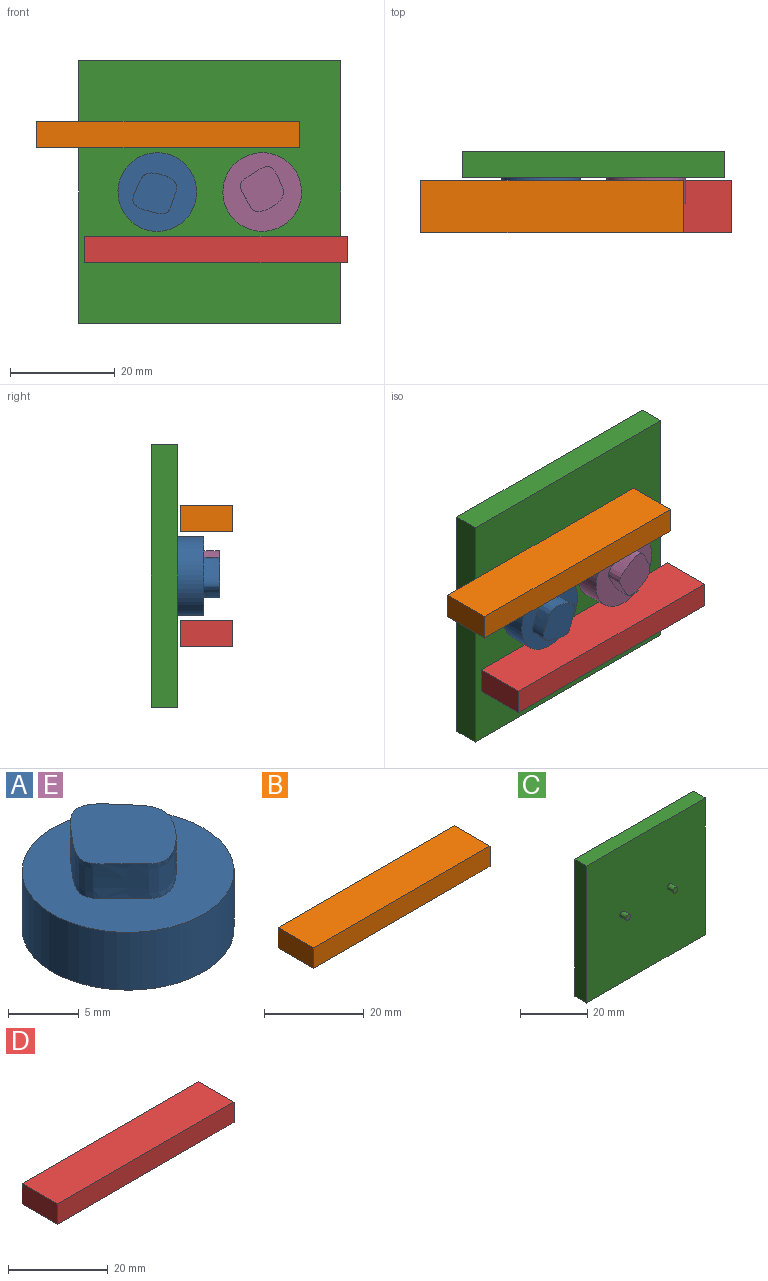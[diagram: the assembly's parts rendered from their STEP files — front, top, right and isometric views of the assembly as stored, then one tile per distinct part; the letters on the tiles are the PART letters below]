
ASSEMBLY  parts=5 mates=4
PART A: 7 faces, bbox 15x15x8 mm
  f0: cylinder r=7.5mm len=15mm, axis (0,0,-1), area 235.6mm2, adj f1,f2
  f1: plane 15x15mm, normal (0,0,1), area 127.5mm2, adj f0,f3
  f2: plane 15x15mm, normal (0,0,-1), area 173.6mm2, adj f0,f5
  f3: extruded ~8.88x8.32mm, area 76.5mm2, adj f1,f4
  f4: plane 9.28x8.73mm, normal (0,0,1), area 49.2mm2, adj f3
  f5: cylinder r=1mm len=2mm, axis (0,0,-1), area 12.6mm2, adj f2,f6
  f6: plane 2x2mm, normal (0,0,-1), area 3.1mm2, adj f5
PART B: 6 faces, bbox 50x10x5 mm
  f0: plane 50x5mm, normal (0,-1,0), area 250mm2, adj f1,f3,f4,f5
  f1: plane 10x5mm, normal (1,0,0), area 50mm2, adj f0,f2,f4,f5
  f2: plane 50x5mm, normal (0,1,0), area 250mm2, adj f1,f3,f4,f5
  f3: plane 10x5mm, normal (-1,0,0), area 50mm2, adj f0,f2,f4,f5
  f4: plane 50x10mm, normal (0,0,1), area 500mm2, adj f0,f1,f2,f3
  f5: plane 50x10mm, normal (0,0,-1), area 500mm2, adj f0,f1,f2,f3
PART C: 10 faces, bbox 50x7.5x50 mm
  f0: plane 50x5mm, normal (0,0,-1), area 250mm2, adj f1,f3,f4,f5
  f1: plane 50x5mm, normal (1,0,0), area 250mm2, adj f0,f2,f4,f5
  f2: plane 50x5mm, normal (0,0,1), area 250mm2, adj f1,f3,f4,f5
  f3: plane 50x5mm, normal (-1,0,0), area 250mm2, adj f0,f2,f4,f5
  f4: plane 50x50mm, normal (0,1,0), area 2500mm2, adj f0,f1,f2,f3
  f5: plane 50x50mm, normal (0,-1,0), area 2493.7mm2, adj f0,f1,f2,f3,f6,f8
  f6: cylinder r=1mm len=2.5mm, axis (0,1,0), area 15.7mm2, adj f5,f7
  f7: plane 2x2mm, normal (0,-1,0), area 3.1mm2, adj f6
  f8: cylinder r=1mm len=2.5mm, axis (0,1,0), area 15.7mm2, adj f5,f9
  f9: plane 2x2mm, normal (0,-1,0), area 3.1mm2, adj f8
PART D: 6 faces, bbox 50x10x5 mm
  f0: plane 10x5mm, normal (1,0,0), area 50mm2, adj f1,f3,f4,f5
  f1: plane 50x5mm, normal (0,1,0), area 250mm2, adj f0,f2,f4,f5
  f2: plane 10x5mm, normal (-1,0,0), area 50mm2, adj f1,f3,f4,f5
  f3: plane 50x5mm, normal (0,-1,0), area 250mm2, adj f0,f2,f4,f5
  f4: plane 50x10mm, normal (0,0,1), area 500mm2, adj f0,f1,f2,f3
  f5: plane 50x10mm, normal (0,0,-1), area 500mm2, adj f0,f1,f2,f3
PART E: same geometry as A
PLACE A rot(axis=(0.41,-0.64,0.64),135deg) t=(-9.78,-1.45,-0.5)mm
PLACE B t=(-7.73,-6.95,8)mm
PLACE C t=(0.22,-1.45,-0.5)mm fixed
PLACE D t=(1.3,-21.95,-14)mm
PLACE E rot(axis=(0.98,0.15,-0.15),91.2deg) t=(10.22,-1.45,-0.5)mm
MATE revolute A.f0 <-> C.f6  axis (0,1,0) through (-9.78,-1.45,-0.5)mm
MATE revolute E.f0 <-> C.f8  axis (0,1,0) through (10.22,-1.45,-0.5)mm
MATE slider C.f1 <-> D.f0  axis (1,0,0) through (25.22,1.05,-0.5)mm
MATE slider C.f1 <-> B.f1  axis (1,0,0) through (25.22,1.05,-0.5)mm
